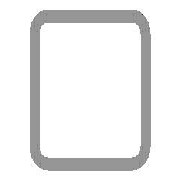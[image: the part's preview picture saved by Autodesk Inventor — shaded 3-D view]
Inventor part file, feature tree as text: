
AUTODESK INVENTOR PART (.ipt)
format: ipt  version: 2025.1 (Build 291241020, 241B)  size: 132,608 bytes
history: native  units: mm (DEFAULTED — no unit token found)
features: other x4, sketch x1, plane x1
ambient origin geometry x8: Origin, YZ Plane, XZ Plane, XY Plane, X Axis, Y Axis, Z Axis, Center Point
bodies: Solid1 (feature_tree), Body (feature_tree)
feature tree (6):
  parser-record x1  (decoder bookkeeping rows leaked as tree rows — omitted from the tree; the rows remain in map.json)
  other  "Driven Length"
  other  "Start Plane"
  other  "End Plane"
  sketch  "Sketch3"  dims[d3=1100.0mm d4=0.0mm d7=6.0mm d9=100.0mm d11=100.0mm d12=3.0mm d13=-0.0mm d14=1100.0mm d15=50.0mm d16=50.0mm d17=90.0deg d18=1100.0mm]
  plane  "Work Plane3"
